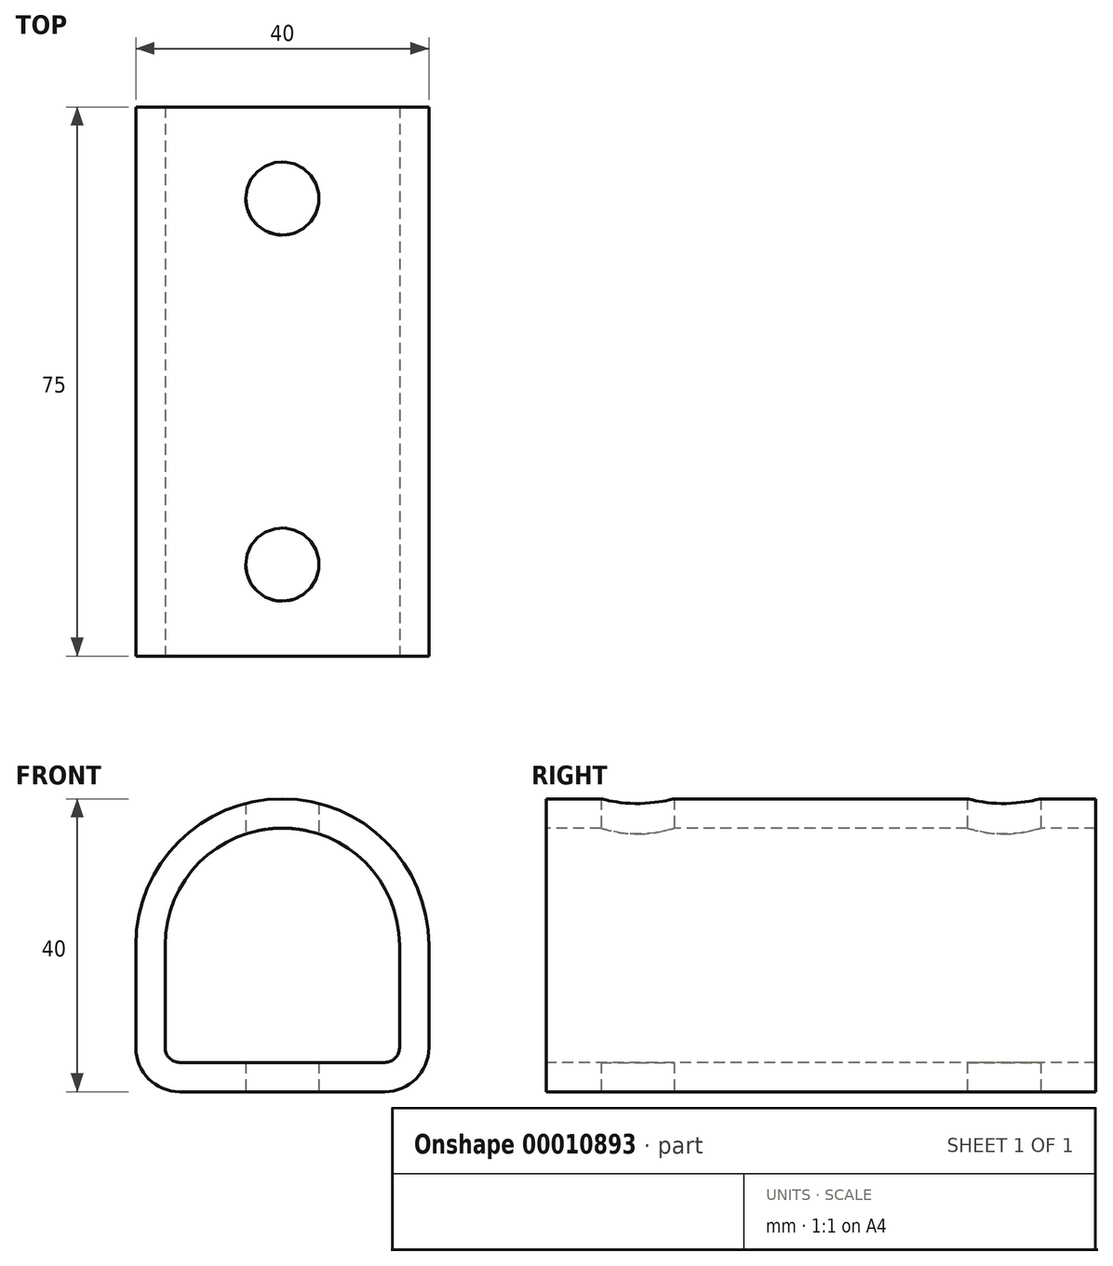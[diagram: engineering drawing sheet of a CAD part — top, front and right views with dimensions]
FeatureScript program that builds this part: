
annotation { "Feature Type Name" : "Feature", "Feature Type Description" : "" }
export const myFeature = defineFeature(function(context is Context, id is Id, definition is map)
    precondition{}
    {
        {
            var Q0;
            Q0=qCreatedBy(makeId("Front.planeOp"),FACE);
            var sketch = newSketch(context, id + "F0", { "sketchPlane" : qUnion([Q0])});
            skLineSegment(sketch, "E0", {"start": v(0, -4.04) * mm, "end": v(0, 46.92) * mm, "construction": true});
            skLineSegment(sketch, "E1", {"start": v(0, 0) * mm, "end": v(14, 0) * mm});
            skLineSegment(sketch, "E2", {"start": v(20, 6) * mm, "end": v(20, 20) * mm});
            skArc(sketch, "E3", {"start": v(20, 20) * mm, "mid": v(14.14, 34.14) * mm, "end": v(0, 40) * mm});
            skArc(sketch, "E4.0.MirrorCS", {"start": v(-20, 20) * mm, "mid": v(-14.14, 34.14) * mm, "end": v(0, 40) * mm});
            skLineSegment(sketch, "E5.0.MirrorCS", {"start": v(-20, 6) * mm, "end": v(-20, 20) * mm});
            skLineSegment(sketch, "E6.0.MirrorCS", {"start": v(0, 0) * mm, "end": v(-14, 0) * mm});
            skPoint(sketch, "E7.visualSharp", {"position": v(-20, 0) * mm});
            skArc(sketch, "E7.filletArc", {"start": v(-20, 6) * mm, "mid": v(-18.24, 1.76) * mm, "end": v(-14, 0) * mm});
            skPoint(sketch, "E8.visualSharp", {"position": v(20, 0) * mm});
            skArc(sketch, "E8.filletArc", {"start": v(14, 0) * mm, "mid": v(18.24, 1.76) * mm, "end": v(20, 6) * mm});
            skArc(sketch, "E9.0", {"start": v(14, 4) * mm, "mid": v(15.41, 4.59) * mm, "end": v(16, 6) * mm});
            skLineSegment(sketch, "E9.1", {"start": v(0, 4) * mm, "end": v(14, 4) * mm});
            skLineSegment(sketch, "E9.2", {"start": v(0, 4) * mm, "end": v(-14, 4) * mm});
            skArc(sketch, "E9.3", {"start": v(-16, 6) * mm, "mid": v(-15.41, 4.59) * mm, "end": v(-14, 4) * mm});
            skLineSegment(sketch, "E9.4", {"start": v(-16, 6) * mm, "end": v(-16, 20) * mm});
            skLineSegment(sketch, "E9.5", {"start": v(16, 6) * mm, "end": v(16, 20) * mm});
            skArc(sketch, "E9.6", {"start": v(-16, 20) * mm, "mid": v(-11.31, 31.31) * mm, "end": v(0, 36) * mm});
            skArc(sketch, "E9.7", {"start": v(16, 20) * mm, "mid": v(11.31, 31.31) * mm, "end": v(0, 36) * mm});
            skSolve(sketch);
        }
        {
            var Q0;
            Q0 = qSketchRegion(id + "F0", true);
            extrude(context, id + "F1", {"entities" : qUnion([Q0]), "oppositeDirection" : true, "depth" : 75 * mm});
        }
        {
            var Q0;
            Q0=qCreatedBy(makeId("Top.planeOp"),FACE);
            var sketch = newSketch(context, id + "F2", { "sketchPlane" : qUnion([Q0])});
            skCircle(sketch, "E10", {"center": v(0, 62.5) * mm, "radius": 5 * mm});
            skCircle(sketch, "E11", {"center": v(0, 12.5) * mm, "radius": 5 * mm});
            skSolve(sketch);
        }
        {
            var Q0;
            Q0 = qSketchRegion(id + "F2", true);
            extrude(context, id + "F3", {"entities" : qUnion([Q0]), "operationType" : NewBodyOperationType.REMOVE, "endBound" : BoundingType.THROUGH_ALL, "depth" : 25 * mm});
        }
    });
